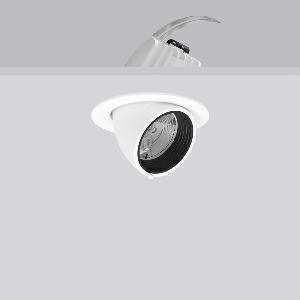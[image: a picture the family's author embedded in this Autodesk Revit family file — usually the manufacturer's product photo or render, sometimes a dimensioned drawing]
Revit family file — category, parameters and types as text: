
# Revit family: golas_mini_911573_002_2_1965
name_source: partatom
category: Lighting Fixtures
units: mm (PartAtom-declared; Revit-internal decimal feet)

## family parameters
Cut with Voids When Loaded = No
Host = Face
Light Source = No
Part Type = Normal
Room Calculation Point = No
Round Connector Dimension = Use Diameter
Shared = No

## types (1)
- GOLAS mini (1 x LED Modul 927, 1850 lm, 2700)
    Apparent Load = 20 VA
    Approval mark = CE
    CIE Flux Codes = 95 100 100 100 100
    Color Rendering = 92
    Color Temperature = 2700
    Default Elevation = 1800 mm
    Description = Series: GOLAS mini
Recessed LED projector for illuminating points to be highlighted. Housing: die-cast aluminium, powder-coated. 356° rotation range and 90° swivel range. Black plastic ring and recessed LED to prevent glare from the side. Optical assembly with lens made of plastic (polycarbonate) for the best homogeneous light distribution - can be changed without tools. Best colour rendering index Ra>90. Suitable for Recessed ceiling mounting. Installation without tools thanks to spring fastening system. Including separate LED converter with connecting cable 600 mm.High quality converter without flickering and stroboscopic effect. Through-wiring box (5 pole) available as accessory. The following accessories can be mounted without use of tools: interchangeable lenses, decorative glasses, honeycomb louvre, clear and frosted diffusers, white interchangeable plastic ring. 
Colour: traffic white, matt (RAL 9016)
Diameter: 143 mm
Height: 3 mm
Cut-out diameter: 133 mm
Recess height: 170 mm
Luminaire: recess height: 115 mm
Lamp: LED
Socket: without socket
Colour temperature: 2700K
Colour rendering index (CRI): 92
System power: 20 W
Rated luminous flux: 1850 lm
Luminous efficiency: 93 lm/W
Control gear: Regulated power supply
Protection class: II
Type of protection: IP 20
    Height = 0 mm  [stored 0 ft]
    Lamp = 1 x LED Modul 927
    Lamp Light Flux = 1850 lm
    Lamp count = 1
    Length = 143 mm
    Lifetime = 50000 h
    Luminous efficacy = 93 lm/W
    Manufacturer = RZB
    ModVariant = No
    Model = 911573.002.2
    Mounting Place = Ceiling, Wall
    Mounting Type = Recessed
    Number of Poles = 1
    OnlyDefault = Yes
    Power Factor = 1
    Product Name = GOLAS mini
    Product group = Recessed projectors
    ProductGroupID = 401
    Protection Class = Protection class II
    Protection Degree = IP 20
    RLX_Detail_Level = 1
    RLX_Emergency_Light_Flux = 0 lm
    RLX_Emergency_Type = 0
    RLX_Emergency_Type_DB = No
    RlxData = <blob elided: 52025 chars, md5=fd3b0e2d>
    Socket = socket
    Standby Power = 0 W
    System Light Flux = 1850 lm
    System Power = 20 W
    Type Comments = Product without accessories
    Type Image = 911438.002.jpg
    URL = http://relux.com
    VarID = ---
    Voltage = 230 V
    Voltage Range = 220-240 V
    Weight = 0.00 kg
    Width = 0 mm  [stored 0 ft]

note: [stored X ft] marks values corroborated as IEEE doubles in the binary element streams (Revit-internal decimal feet)

## geometry (parser evidence)
native form markers: Blend x4, Sweep x13
no freeform markers — native parametric forms only
